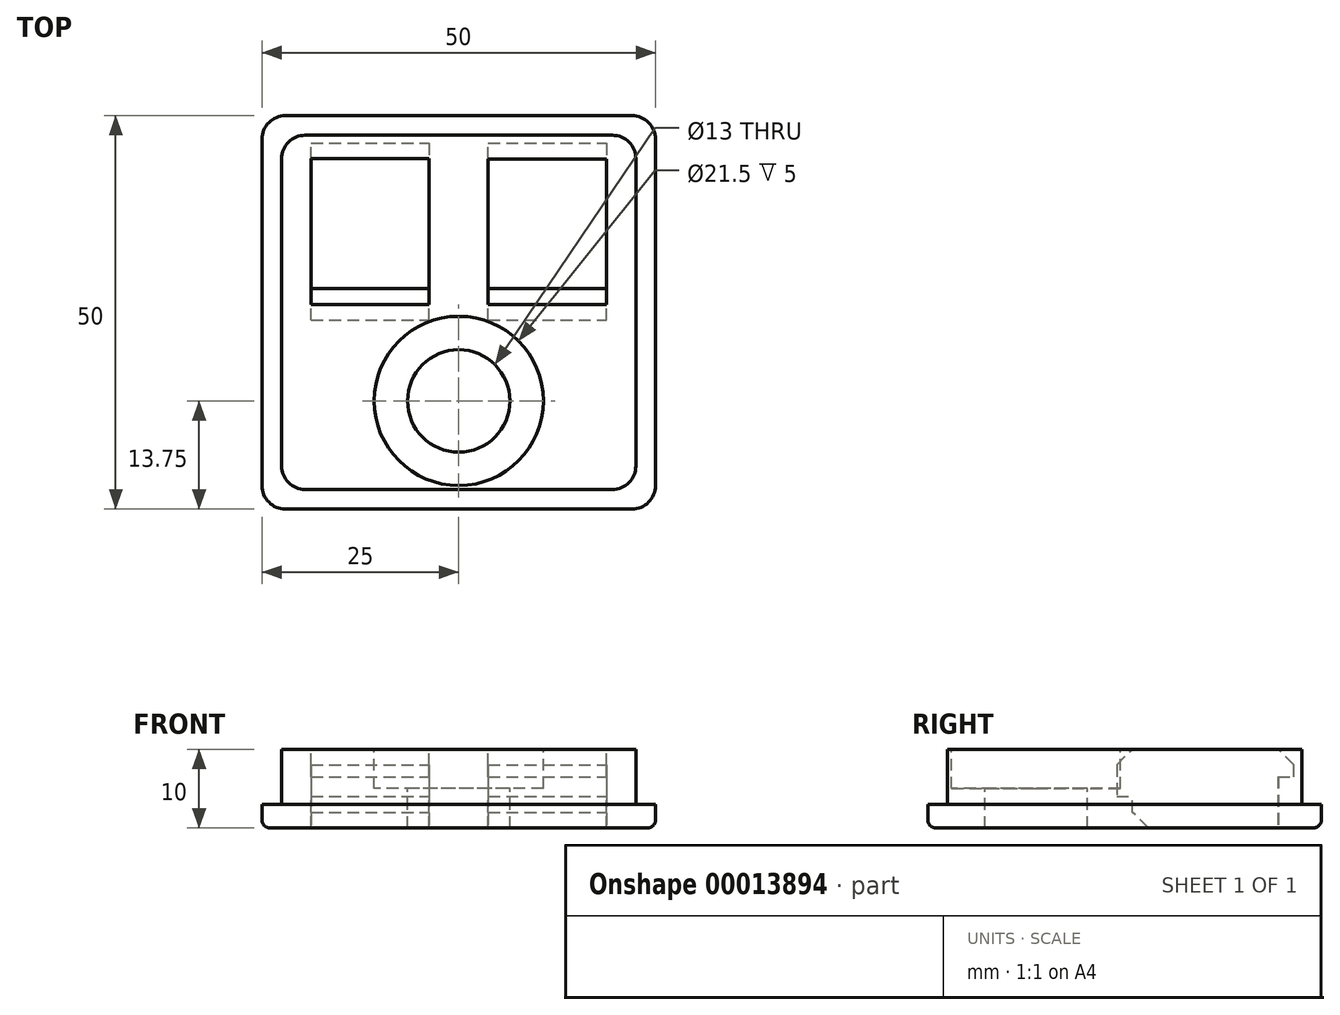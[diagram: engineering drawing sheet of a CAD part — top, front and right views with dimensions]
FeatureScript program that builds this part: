
annotation { "Feature Type Name" : "Feature", "Feature Type Description" : "" }
export const myFeature = defineFeature(function(context is Context, id is Id, definition is map)
    precondition{}
    {
        {
            var Q0;
            Q0=qCreatedBy(makeId("Top.planeOp"),FACE);
            var sketch = newSketch(context, id + "F0", { "sketchPlane" : qUnion([Q0])});
            skLineSegment(sketch, "E0.bottom", {"start": v(25, -25) * mm, "end": v(-25, -25) * mm});
            skLineSegment(sketch, "E0.top", {"start": v(25, 25) * mm, "end": v(-25, 25) * mm});
            skLineSegment(sketch, "E0.left", {"start": v(25, -25) * mm, "end": v(25, 25) * mm});
            skLineSegment(sketch, "E0.right", {"start": v(-25, -25) * mm, "end": v(-25, 25) * mm});
            skPoint(sketch, "E0.middle", {"position": v(0, 0) * mm});
            skLineSegment(sketch, "E1.bottom", {"start": v(22.5, -22.5) * mm, "end": v(-22.5, -22.5) * mm});
            skLineSegment(sketch, "E1.top", {"start": v(22.5, 22.5) * mm, "end": v(-22.5, 22.5) * mm});
            skLineSegment(sketch, "E1.left", {"start": v(22.5, -22.5) * mm, "end": v(22.5, 22.5) * mm});
            skLineSegment(sketch, "E1.right", {"start": v(-22.5, -22.5) * mm, "end": v(-22.5, 22.5) * mm});
            skLineSegment(sketch, "E2", {"start": v(0, 0) * mm, "end": v(0, 22.5) * mm, "construction": true});
            skLineSegment(sketch, "E3", {"start": v(22.5, 11.25) * mm, "end": v(0, 11.25) * mm, "construction": true});
            skPoint(sketch, "E3.startSnap0", {"position": v(0, 11.25) * mm});
            skLineSegment(sketch, "E4", {"start": v(0, 11.25) * mm, "end": v(-22.5, 11.28) * mm, "construction": true});
            skLineSegment(sketch, "E5.bottom", {"start": v(18.75, 3) * mm, "end": v(3.75, 3) * mm});
            skLineSegment(sketch, "E5.top", {"start": v(18.75, 19.5) * mm, "end": v(3.75, 19.5) * mm});
            skLineSegment(sketch, "E5.left", {"start": v(18.75, 3) * mm, "end": v(18.75, 19.5) * mm});
            skLineSegment(sketch, "E5.right", {"start": v(3.75, 3) * mm, "end": v(3.75, 19.5) * mm});
            skPoint(sketch, "E5.middle", {"position": v(11.25, 11.25) * mm});
            skLineSegment(sketch, "E6.bottom", {"start": v(-3.75, 3.01) * mm, "end": v(-18.75, 3.01) * mm});
            skLineSegment(sketch, "E6.top", {"start": v(-3.75, 19.51) * mm, "end": v(-18.75, 19.51) * mm});
            skLineSegment(sketch, "E6.left", {"start": v(-3.75, 3.01) * mm, "end": v(-3.75, 19.51) * mm});
            skLineSegment(sketch, "E6.right", {"start": v(-18.75, 3.01) * mm, "end": v(-18.75, 19.51) * mm});
            skPoint(sketch, "E6.middle", {"position": v(-11.25, 11.26) * mm});
            skLineSegment(sketch, "E7", {"start": v(0, 0) * mm, "end": v(0, -22.5) * mm, "construction": true});
            skPoint(sketch, "E8", {"position": v(0, -11.25) * mm});
            skSolve(sketch);
        }
        {
            var Q0;
            Q0=makeQuery(id+"F0.imprint","IMPRINT",FACE,{"disambiguationData":[TD([[makeQuery(id+"F0.imprint","IMPRINT",EDGE,{"derivedFrom":sQuery(id+"F0.wireOp",EDGE,"E0.bottom")}),-1.0]])]});
            var Q1;
            Q1=makeQuery(id+"F0.imprint","IMPRINT",FACE,{"disambiguationData":[TD([[makeQuery(id+"F0.imprint","IMPRINT",EDGE,{"derivedFrom":sQuery(id+"F0.wireOp",EDGE,"E1.bottom")}),-1.0]])]});
            extrude(context, id + "F1", {"entities" : qUnion([Q0, Q1]), "depth" : 3 * mm});
        }
        {
            var Q0;
            Q0=makeQuery(id+"F0.imprint","IMPRINT",FACE,{"disambiguationData":[TD([[makeQuery(id+"F0.imprint","IMPRINT",EDGE,{"derivedFrom":sQuery(id+"F0.wireOp",EDGE,"E1.bottom")}),-1.0]])]});
            extrude(context, id + "F2", {"entities" : qUnion([Q0]), "operationType" : NewBodyOperationType.ADD, "depth" : 10 * mm});
        }
        {
            var Q0;
            Q0=makeQuery(id+"F2.opExtrude","CAP_FACE",FACE,{"disambiguationData":[OSD([sQuery(id+"F0.wireOp",EDGE,"E1.bottom"),sQuery(id+"F0.wireOp",EDGE,"E1.top"),sQuery(id+"F0.wireOp",EDGE,"E1.left"),sQuery(id+"F0.wireOp",EDGE,"E1.right"),sQuery(id+"F0.wireOp",EDGE,"E5.bottom"),sQuery(id+"F0.wireOp",EDGE,"E5.top"),sQuery(id+"F0.wireOp",EDGE,"E5.left"),sQuery(id+"F0.wireOp",EDGE,"E5.right"),sQuery(id+"F0.wireOp",EDGE,"E6.bottom"),sQuery(id+"F0.wireOp",EDGE,"E6.top"),sQuery(id+"F0.wireOp",EDGE,"E6.left"),sQuery(id+"F0.wireOp",EDGE,"E6.right")])],"isStart":false});
            var sketch = newSketch(context, id + "F3", { "sketchPlane" : qUnion([Q0])});
            skPoint(sketch, "E9.0", {"position": v(0, -11.25) * mm});
            skSolve(sketch);
        }
        {
            var Q0;
            Q0=sQuery(id+"F3.wireOp",VERTEX,"E9.0");
            var Q1;
            Q1=makeQuery(id+"F1.opExtrude","SWEPT_BODY",BODY,{"disambiguationData":[OSD([sQuery(id+"F0.wireOp",EDGE,"E0.bottom"),sQuery(id+"F0.wireOp",EDGE,"E0.top"),sQuery(id+"F0.wireOp",EDGE,"E0.left"),sQuery(id+"F0.wireOp",EDGE,"E0.right"),sQuery(id+"F0.wireOp",EDGE,"E5.bottom"),sQuery(id+"F0.wireOp",EDGE,"E5.top"),sQuery(id+"F0.wireOp",EDGE,"E5.left"),sQuery(id+"F0.wireOp",EDGE,"E5.right"),sQuery(id+"F0.wireOp",EDGE,"E6.bottom"),sQuery(id+"F0.wireOp",EDGE,"E6.top"),sQuery(id+"F0.wireOp",EDGE,"E6.left"),sQuery(id+"F0.wireOp",EDGE,"E6.right")])]});
            hole(context, id + "F4", {"style" : HoleStyle.C_BORE, "endStyle" : HoleEndStyle.THROUGH, "holeDiameter" : 13 * mm, "cBoreDiameter" : 21.5 * mm, "cBoreDepth" : 5 * mm, "locations" : qUnion([Q0]), "scope" : qUnion([Q1]), "isTappedThrough" : true});
        }
        {
            var Q0;
            {var subQ0=sQuery(id+"F0.wireOp",EDGE,"E5.left");Q0=makeQuery(id+"F2.boolean.opBoolean","MERGE",FACE,{"derivedFrom":[makeQuery(id+"F1.opExtrude","SWEPT_FACE",FACE,{"disambiguationData":[OSD([subQ0])]}),makeQuery(id+"F2.opExtrude","SWEPT_FACE",FACE,{"disambiguationData":[OSD([subQ0])]})]});}
            var sketch = newSketch(context, id + "F5", { "sketchPlane" : qUnion([Q0])});
            skLineSegment(sketch, "E10", {"start": v(1, 8) * mm, "end": v(1, 4) * mm});
            skLineSegment(sketch, "E11", {"start": v(1, 4) * mm, "end": v(-1, 4) * mm});
            skLineSegment(sketch, "E12", {"start": v(-3, 0) * mm, "end": v(-19.5, 0) * mm});
            skLineSegment(sketch, "E13", {"start": v(-19.5, 0) * mm, "end": v(-19.5, 6.5) * mm});
            skLineSegment(sketch, "E14", {"start": v(-19.5, 6.5) * mm, "end": v(-21.5, 6.5) * mm});
            skLineSegment(sketch, "E15", {"start": v(-21.5, 6.5) * mm, "end": v(-21.5, 8) * mm});
            skLineSegment(sketch, "E16", {"start": v(-21.5, 8) * mm, "end": v(-19.5, 10) * mm});
            skLineSegment(sketch, "E17", {"start": v(-19.5, 10) * mm, "end": v(-3, 10) * mm});
            skLineSegment(sketch, "E18", {"start": v(1, 8) * mm, "end": v(-1, 10) * mm});
            skLineSegment(sketch, "E19", {"start": v(-1, 10) * mm, "end": v(-3, 10) * mm});
            skLineSegment(sketch, "E20", {"start": v(-3, 0) * mm, "end": v(-1, 2) * mm});
            skLineSegment(sketch, "E21", {"start": v(-1, 2) * mm, "end": v(-1, 4) * mm});
            skPoint(sketch, "E22.orphan", {"position": v(-3, 4) * mm});
            skSolve(sketch);
        }
        {
            var Q0;
            Q0 = qSketchRegion(id + "F5", true);
            var Q1;
            {var subQ0=sQuery(id+"F0.wireOp",EDGE,"E5.right");Q1=makeQuery(id+"F2.boolean.opBoolean","MERGE",FACE,{"derivedFrom":[makeQuery(id+"F1.opExtrude","SWEPT_FACE",FACE,{"disambiguationData":[OSD([subQ0])]}),makeQuery(id+"F2.opExtrude","SWEPT_FACE",FACE,{"disambiguationData":[OSD([subQ0])]})]});}
            extrude(context, id + "F6", {"entities" : qUnion([Q0]), "operationType" : NewBodyOperationType.REMOVE, "endBound" : BoundingType.UP_TO_SURFACE, "endBoundEntityFace" : qUnion([Q1]), "depth" : 25 * mm});
        }
        {
            var Q0;
            Q0 = qSketchRegion(id + "F5", true);
            var Q1;
            {var subQ0=sQuery(id+"F0.wireOp",EDGE,"E6.right");Q1=makeQuery(id+"F2.boolean.opBoolean","MERGE",FACE,{"derivedFrom":[makeQuery(id+"F1.opExtrude","SWEPT_FACE",FACE,{"disambiguationData":[OSD([subQ0])]}),makeQuery(id+"F2.opExtrude","SWEPT_FACE",FACE,{"disambiguationData":[OSD([subQ0])]})]});}
            var Q2;
            {var subQ0=sQuery(id+"F0.wireOp",EDGE,"E6.left");Q2=makeQuery(id+"F2.boolean.opBoolean","MERGE",FACE,{"derivedFrom":[makeQuery(id+"F1.opExtrude","SWEPT_FACE",FACE,{"disambiguationData":[OSD([subQ0])]}),makeQuery(id+"F2.opExtrude","SWEPT_FACE",FACE,{"disambiguationData":[OSD([subQ0])]})]});}
            extrude(context, id + "F7", {"entities" : qUnion([Q0]), "operationType" : NewBodyOperationType.REMOVE, "endBound" : BoundingType.UP_TO_SURFACE, "endBoundEntityFace" : qUnion([Q1]), "depth" : 25 * mm, "hasSecondDirection" : true, "secondDirectionBound" : SecondDirectionBoundingType.UP_TO_SURFACE, "secondDirectionOppositeDirection" : false, "secondDirectionBoundEntityFace" : qUnion([Q2]), "secondDirectionDepth" : 25 * mm});
        }
        {
            var Q0;
            Q0=makeQuery(id+"F2.opExtrude","SWEPT_EDGE",EDGE,{"disambiguationData":[OSD([sQuery(id+"F0.wireOp",EDGE,"E1.top"),sQuery(id+"F0.wireOp",EDGE,"E1.left")])]});
            var Q1;
            Q1=makeQuery(id+"F2.opExtrude","SWEPT_EDGE",EDGE,{"disambiguationData":[OSD([sQuery(id+"F0.wireOp",EDGE,"E1.top"),sQuery(id+"F0.wireOp",EDGE,"E1.right")])]});
            var Q2;
            Q2=makeQuery(id+"F2.opExtrude","SWEPT_EDGE",EDGE,{"disambiguationData":[OSD([sQuery(id+"F0.wireOp",EDGE,"E1.bottom"),sQuery(id+"F0.wireOp",EDGE,"E1.left")])]});
            var Q3;
            Q3=makeQuery(id+"F2.opExtrude","SWEPT_EDGE",EDGE,{"disambiguationData":[OSD([sQuery(id+"F0.wireOp",EDGE,"E1.bottom"),sQuery(id+"F0.wireOp",EDGE,"E1.right")])]});
            var Q4;
            Q4=makeQuery(id+"F1.opExtrude","SWEPT_EDGE",EDGE,{"disambiguationData":[OSD([sQuery(id+"F0.wireOp",EDGE,"E0.top"),sQuery(id+"F0.wireOp",EDGE,"E0.right")])]});
            var Q5;
            Q5=makeQuery(id+"F1.opExtrude","SWEPT_EDGE",EDGE,{"disambiguationData":[OSD([sQuery(id+"F0.wireOp",EDGE,"E0.top"),sQuery(id+"F0.wireOp",EDGE,"E0.left")])]});
            var Q6;
            Q6=makeQuery(id+"F1.opExtrude","SWEPT_EDGE",EDGE,{"disambiguationData":[OSD([sQuery(id+"F0.wireOp",EDGE,"E0.bottom"),sQuery(id+"F0.wireOp",EDGE,"E0.right")])]});
            var Q7;
            Q7=makeQuery(id+"F1.opExtrude","SWEPT_EDGE",EDGE,{"disambiguationData":[OSD([sQuery(id+"F0.wireOp",EDGE,"E0.bottom"),sQuery(id+"F0.wireOp",EDGE,"E0.left")])]});
            fillet(context, id + "F8", {"entities" : qUnion([Q0, Q1, Q2, Q3, Q4, Q5, Q6, Q7]), "radius" : 3 * mm, "tangentPropagation" : true, "allowEdgeOverflow" : false});
        }
        {
            var Q0;
            Q0=makeQuery(id+"F1.opExtrude","CAP_EDGE",EDGE,{"disambiguationData":[OSD([sQuery(id+"F0.wireOp",EDGE,"E0.top")])],"isStart":true});
            fillet(context, id + "F9", {"entities" : qUnion([Q0]), "radius" : 1 * mm, "tangentPropagation" : true, "allowEdgeOverflow" : false});
        }
    });
